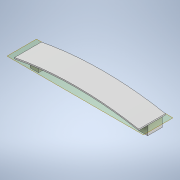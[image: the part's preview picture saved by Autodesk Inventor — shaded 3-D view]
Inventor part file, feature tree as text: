
AUTODESK INVENTOR PART (.ipt)
format: ipt  version: 2020.2 (Build 242310000, 310)  size: 140,800 bytes
history: native  units: mm
features: extrude x3, sketch x3, other x1
ambient origin geometry x8: Origin, YZ Plane, XZ Plane, XY Plane, X Axis, Y Axis, Z Axis, Center Point
bodies: Solide1 (feature_tree)
feature tree (7):
  extrude  "Extrusion1"  Depth=785.7mm
  other  "Plan de construction1"
  extrude  "Extrusion2"  Depth=3.0mm
  extrude  "Extrusion3"  Depth=14.3mm
  sketch  "Esquisse1"
  sketch  "Esquisse4"
  sketch  "Esquisse5"
